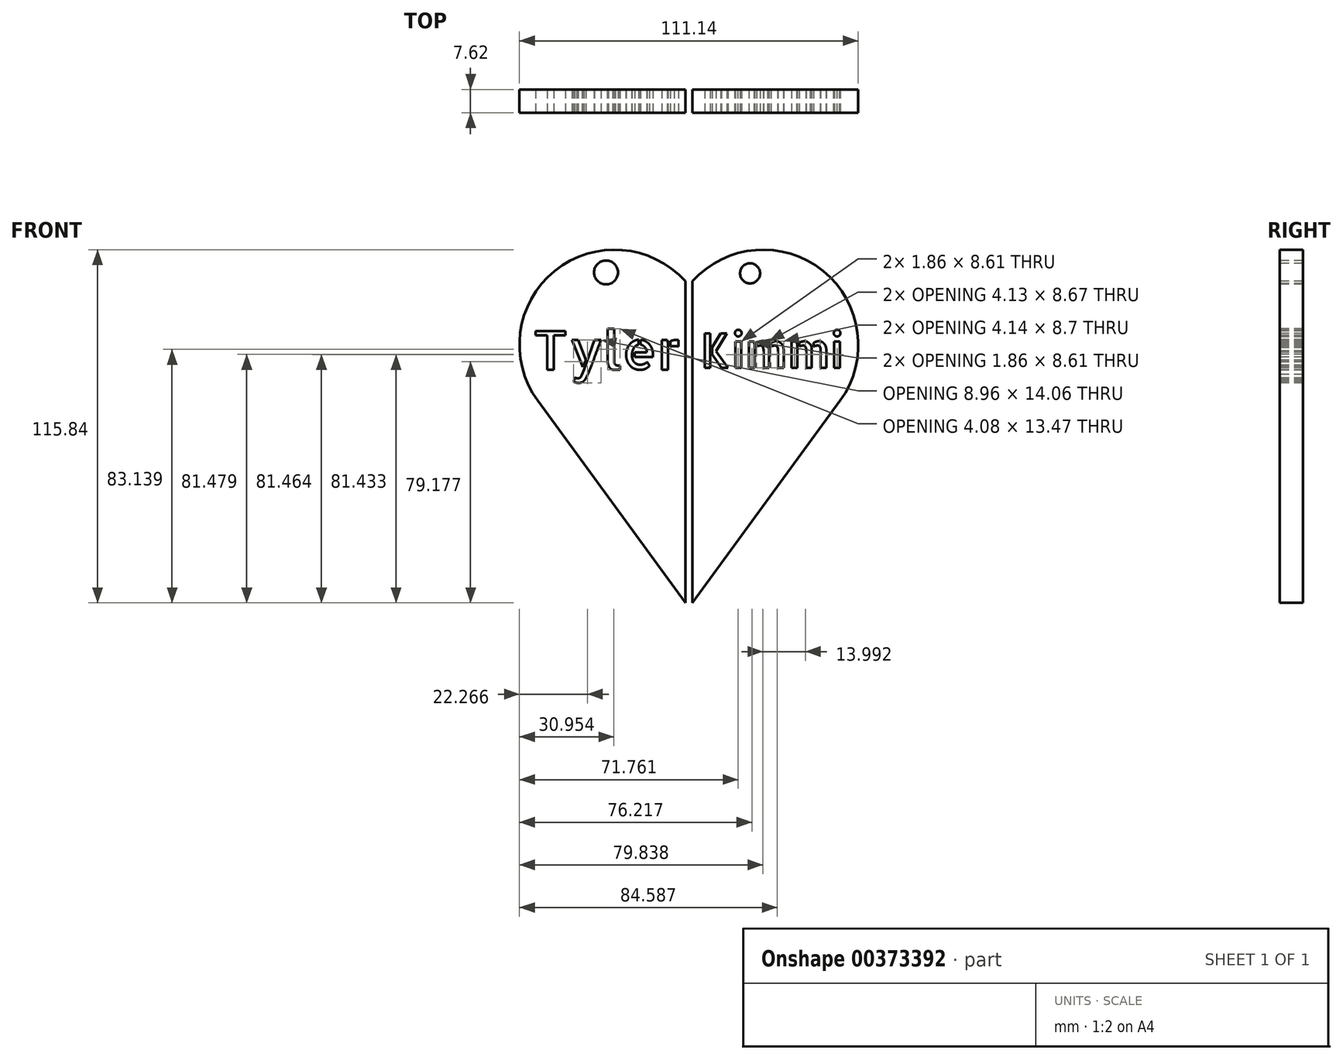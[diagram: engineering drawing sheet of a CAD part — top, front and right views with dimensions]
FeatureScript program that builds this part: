
annotation { "Feature Type Name" : "Feature", "Feature Type Description" : "" }
export const myFeature = defineFeature(function(context is Context, id is Id, definition is map)
    precondition{}
    {
        {
            var Q0;
            Q0=qCreatedBy(makeId("Front.planeOp"),FACE);
            var sketch = newSketch(context, id + "F0", { "sketchPlane" : qUnion([Q0])});
            skArc(sketch, "E0", {"start": v(49.57, 16.2) * mm, "mid": v(43.3, 59.38) * mm, "end": v(0, 54.04) * mm});
            skLineSegment(sketch, "E1", {"start": v(0, -51.66) * mm, "end": v(49.57, 16.2) * mm});
            skArc(sketch, "E2.MirrorCS", {"start": v(-49.57, 16.2) * mm, "mid": v(-43.3, 59.38) * mm, "end": v(0, 54.04) * mm});
            skLineSegment(sketch, "E3.MirrorCS", {"start": v(0, -51.66) * mm, "end": v(-49.57, 16.2) * mm});
            skSolve(sketch);
        }
        {
            var Q0;
            Q0 = qSketchRegion(id + "F0", true);
            extrude(context, id + "F1", {"entities" : qUnion([Q0]), "depth" : 7.62 * mm});
        }
        {
            var Q0;
            Q0=makeQuery(id+"F1.opExtrude","CAP_FACE",FACE,{"disambiguationData":[OSD([sQuery(id+"F0.wireOp",EDGE,"E0"),sQuery(id+"F0.wireOp",EDGE,"E1"),sQuery(id+"F0.wireOp",EDGE,"E2.MirrorCS"),sQuery(id+"F0.wireOp",EDGE,"E3.MirrorCS")])],"isStart":false});
            var sketch = newSketch(context, id + "F2", { "sketchPlane" : qUnion([Q0])});
            skText(sketch, "E4", { "text": "Kimmi", "fontName": "AllertaStencil-Regular.ttf"});
            skText(sketch, "E5", { "text": "Tyler", "fontName": "AllertaStencil-Regular.ttf"});
            const initialGuessF2  = {"E4": [0.00377, 0.02707, 1, 0, 0.01125], "E5": [-0.0511, 0.02643, 1, 0, 0.0127]};
            skSetInitialGuess(sketch, initialGuessF2);
            skSolve(sketch);
        }
        {
            var Q0;
            Q0 = qSketchRegion(id + "F2", true);
            extrude(context, id + "F3", {"entities" : qUnion([Q0]), "operationType" : NewBodyOperationType.REMOVE, "oppositeDirection" : true, "depth" : 7.62 * mm});
        }
        {
            var Q0;
            Q0=makeQuery(id+"F1.opExtrude","CAP_FACE",FACE,{"disambiguationData":[OSD([sQuery(id+"F0.wireOp",EDGE,"E0"),sQuery(id+"F0.wireOp",EDGE,"E1"),sQuery(id+"F0.wireOp",EDGE,"E2.MirrorCS"),sQuery(id+"F0.wireOp",EDGE,"E3.MirrorCS")])],"isStart":false});
            var sketch = newSketch(context, id + "F4", { "sketchPlane" : qUnion([Q0])});
            skLineSegment(sketch, "E6", {"start": v(-1.17, 55.42) * mm, "end": v(-1.17, -50.06) * mm});
            skLineSegment(sketch, "E7", {"start": v(1.17, 55.42) * mm, "end": v(1.17, -50.06) * mm});
            skLineSegment(sketch, "E8", {"start": v(1.17, -50.06) * mm, "end": v(0, -51.66) * mm});
            skLineSegment(sketch, "E9", {"start": v(0, -51.66) * mm, "end": v(-1.17, -50.06) * mm});
            skLineSegment(sketch, "E10", {"start": v(0, 54.04) * mm, "end": v(1.17, 55.42) * mm});
            skLineSegment(sketch, "E11", {"start": v(-1.17, 55.42) * mm, "end": v(1.17, 55.42) * mm});
            skLineSegment(sketch, "E12", {"start": v(0, 54.04) * mm, "end": v(-1.17, 55.42) * mm});
            skSolve(sketch);
        }
        {
            var Q0;
            Q0 = qSketchRegion(id + "F4", true);
            extrude(context, id + "F5", {"entities" : qUnion([Q0]), "operationType" : NewBodyOperationType.REMOVE, "oppositeDirection" : true, "depth" : 7.62 * mm});
        }
        {
            var Q0;
            {var subQ0=sQuery(id+"F0.wireOp",EDGE,"E1");var subQ1=sQuery(id+"F0.wireOp",EDGE,"E0");Q0=makeQuery(id+"F5.boolean.opBoolean","SPLIT",FACE,{"disambiguationData":[TD([makeQuery(id+"F1.opExtrude","SWEPT_FACE",FACE,{"disambiguationData":[OSD([subQ1])]})])],"derivedFrom":makeQuery(id+"F1.opExtrude","CAP_FACE",FACE,{"disambiguationData":[OSD([subQ1,subQ0,sQuery(id+"F0.wireOp",EDGE,"E2.MirrorCS"),sQuery(id+"F0.wireOp",EDGE,"E3.MirrorCS")])],"isStart":false})});}
            var sketch = newSketch(context, id + "F6", { "sketchPlane" : qUnion([Q0])});
            skCircle(sketch, "E13", {"center": v(-23.48, 58.03) * mm, "radius": 3.52 * mm});
            skCircle(sketch, "E14", {"center": v(20.07, 58.03) * mm, "radius": 3.28 * mm});
            skCircle(sketch, "E15", {"center": v(20.07, 58.03) * mm, "radius": 3.31 * mm});
            skCircle(sketch, "E16", {"center": v(-23.48, 58.03) * mm, "radius": 3.62 * mm});
            skSolve(sketch);
        }
        {
            var Q0;
            Q0=makeQuery(id+"F6.imprint","IMPRINT",FACE,{"disambiguationData":[TD([[makeQuery(id+"F6.imprint","IMPRINT",EDGE,{"derivedFrom":sQuery(id+"F6.wireOp",EDGE,"E14")}),1.0]])]});
            extrude(context, id + "F7", {"entities" : qUnion([Q0]), "operationType" : NewBodyOperationType.REMOVE, "oppositeDirection" : true, "depth" : 25.4 * mm});
        }
        {
            var Q0;
            {var subQ0=sQuery(id+"F0.wireOp",EDGE,"E3.MirrorCS");var subQ1=sQuery(id+"F0.wireOp",EDGE,"E2.MirrorCS");Q0=makeQuery(id+"F5.boolean.opBoolean","SPLIT",FACE,{"disambiguationData":[TD([makeQuery(id+"F1.opExtrude","SWEPT_FACE",FACE,{"disambiguationData":[OSD([subQ1])]})])],"derivedFrom":makeQuery(id+"F1.opExtrude","CAP_FACE",FACE,{"disambiguationData":[OSD([sQuery(id+"F0.wireOp",EDGE,"E0"),sQuery(id+"F0.wireOp",EDGE,"E1"),subQ1,subQ0])],"isStart":false})});}
            var sketch = newSketch(context, id + "F8", { "sketchPlane" : qUnion([Q0])});
            skCircle(sketch, "E17", {"center": v(-27.19, 58.33) * mm, "radius": 3.93 * mm});
            skSolve(sketch);
        }
        {
            var Q0;
            Q0 = qSketchRegion(id + "F8", true);
            extrude(context, id + "F9", {"entities" : qUnion([Q0]), "operationType" : NewBodyOperationType.REMOVE, "oppositeDirection" : true, "depth" : 25.4 * mm});
        }
    });
